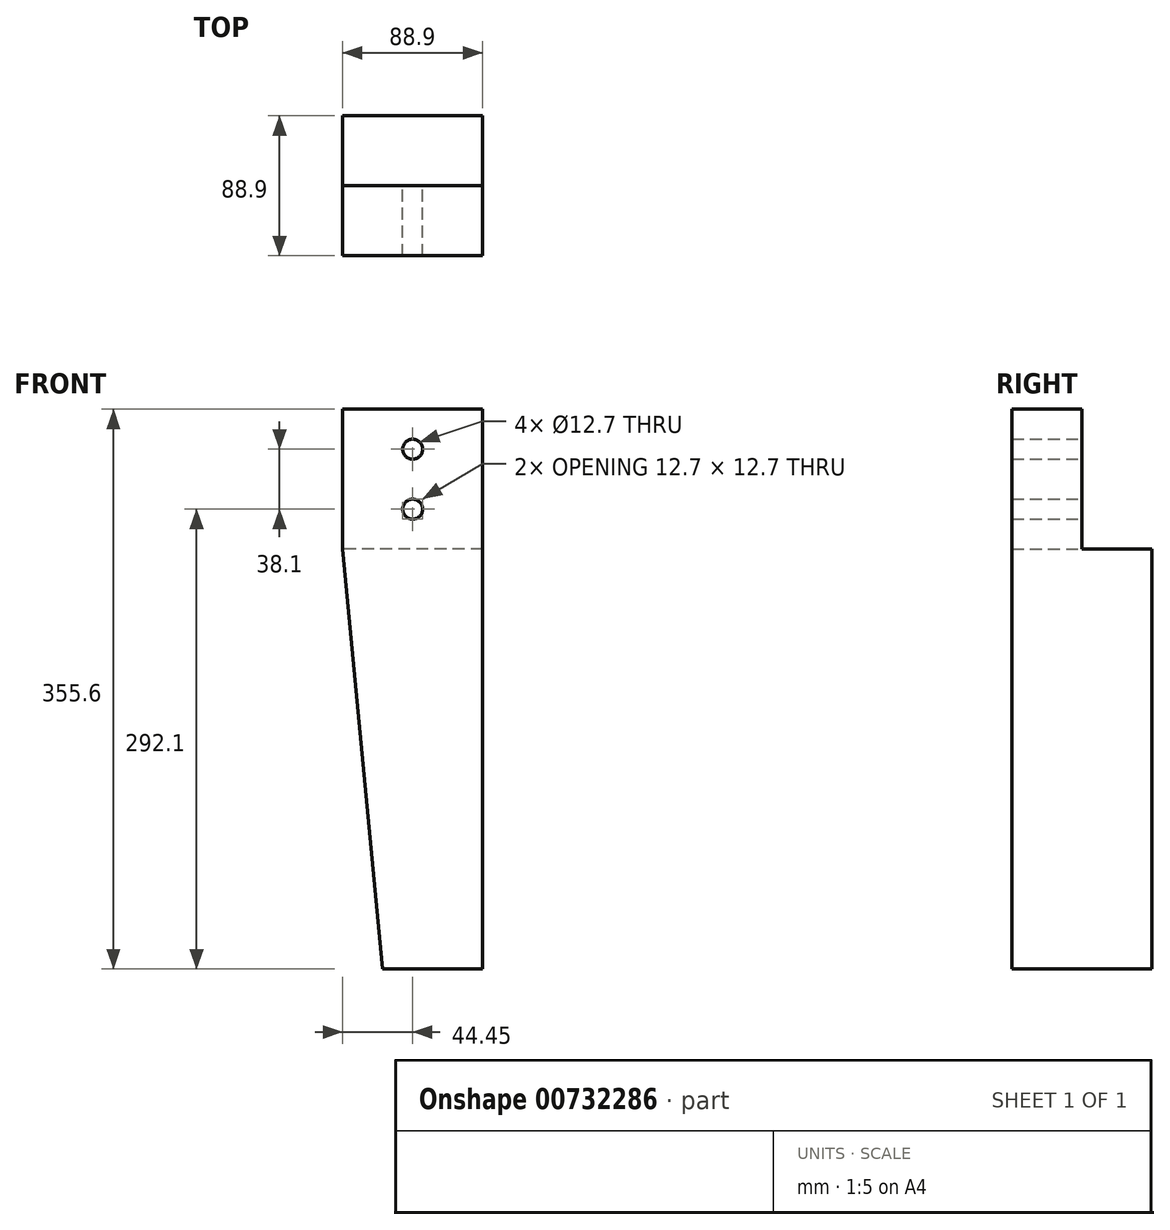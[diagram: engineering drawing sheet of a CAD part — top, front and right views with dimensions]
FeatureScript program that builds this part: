
annotation { "Feature Type Name" : "Feature", "Feature Type Description" : "" }
export const myFeature = defineFeature(function(context is Context, id is Id, definition is map)
    precondition{}
    {
        {
            var Q0;
            Q0=qCreatedBy(makeId("Front.planeOp"),FACE);
            var sketch = newSketch(context, id + "F0", { "sketchPlane" : qUnion([Q0])});
            skLineSegment(sketch, "E0.bottom", {"start": v(44.45, 177.8) * mm, "end": v(-44.45, 177.8) * mm});
            skLineSegment(sketch, "E0.top", {"start": v(44.45, -177.8) * mm, "end": v(-44.45, -177.8) * mm});
            skLineSegment(sketch, "E0.left", {"start": v(44.45, 177.8) * mm, "end": v(44.45, -177.8) * mm});
            skLineSegment(sketch, "E0.right", {"start": v(-44.45, 177.8) * mm, "end": v(-44.45, -177.8) * mm});
            skPoint(sketch, "E0.middle", {"position": v(0, 0) * mm});
            skLineSegment(sketch, "E1", {"start": v(-44.45, 88.9) * mm, "end": v(44.45, 88.9) * mm, "construction": true});
            skLineSegment(sketch, "E2", {"start": v(-19.05, 177.8) * mm, "end": v(-19.05, -177.8) * mm, "construction": true});
            skLineSegment(sketch, "E3", {"start": v(-44.45, 88.9) * mm, "end": v(-19.05, -177.8) * mm});
            skLineSegment(sketch, "E4", {"start": v(-44.45, 133.35) * mm, "end": v(44.45, 133.35) * mm, "construction": true});
            skLineSegment(sketch, "E5", {"start": v(-44.45, 152.4) * mm, "end": v(44.45, 152.4) * mm, "construction": true});
            skLineSegment(sketch, "E6", {"start": v(-44.45, 114.3) * mm, "end": v(44.45, 114.3) * mm, "construction": true});
            skLineSegment(sketch, "E7", {"start": v(0, 177.8) * mm, "end": v(0, 88.9) * mm, "construction": true});
            skCircle(sketch, "E8", {"center": v(0, 152.4) * mm, "radius": 6.35 * mm});
            skCircle(sketch, "E9", {"center": v(0, 114.3) * mm, "radius": 6.35 * mm});
            skLineSegment(sketch, "E10", {"start": v(19.05, 88.9) * mm, "end": v(19.05, -177.8) * mm, "construction": true});
            skSolve(sketch);
        }
        {
            var Q0;
            {var subQ1=sQuery(id+"F0.wireOp",EDGE,"E0.bottom");Q0=makeQuery(id+"F0.imprint","IMPRINT",FACE,{"disambiguationData":[TD([[makeQuery(id+"F0.imprint","IMPRINT",EDGE,{"derivedFrom":subQ1}),1.0]])]});}
            extrude(context, id + "F1", {"entities" : qUnion([Q0]), "depth" : 88.9 * mm, "offsetDistance" : 25.4 * mm});
        }
        {
            var Q0;
            Q0=makeQuery(id+"F1.opExtrude","SWEPT_FACE",FACE,{"disambiguationData":[OSD([sQuery(id+"F0.wireOp",EDGE,"E0.right")])]});
            var sketch = newSketch(context, id + "F2", { "sketchPlane" : qUnion([Q0])});
            skLineSegment(sketch, "E11", {"start": v(44.45, 177.8) * mm, "end": v(44.45, 88.9) * mm});
            skSolve(sketch);
        }
        {
            var Q0;
            {var subQ0=sQuery(id+"F2.wireOp",EDGE,"E11");Q0=makeQuery(id+"F2.imprint","IMPRINT",FACE,{"disambiguationData":[TD([[makeQuery(id+"F2.imprint","IMPRINT",EDGE,{"derivedFrom":subQ0}),-1.0]])]});}
            extrude(context, id + "F3", {"entities" : qUnion([Q0]), "operationType" : NewBodyOperationType.REMOVE, "oppositeDirection" : true, "depth" : 101.6 * mm, "offsetDistance" : 25.4 * mm});
        }
        {
            var Q0;
            Q0=makeQuery(id+"F1.opExtrude","SWEPT_BODY",BODY,{"disambiguationData":[OSD([sQuery(id+"F0.wireOp",EDGE,"E0.bottom"),sQuery(id+"F0.wireOp",EDGE,"E0.top"),sQuery(id+"F0.wireOp",EDGE,"E0.left"),sQuery(id+"F0.wireOp",EDGE,"E0.right"),sQuery(id+"F0.wireOp",EDGE,"E3"),sQuery(id+"F0.wireOp",EDGE,"E8"),sQuery(id+"F0.wireOp",EDGE,"E9")])]});
            transform(context, id + "F4", {"entities" : qUnion([Q0]), "transformType" : TransformType.TRANSLATION_3D, "dx" : 0 * mm, "dy" : 0 * mm, "dz" : 0 * mm, "makeCopy" : true});
        }
    });
